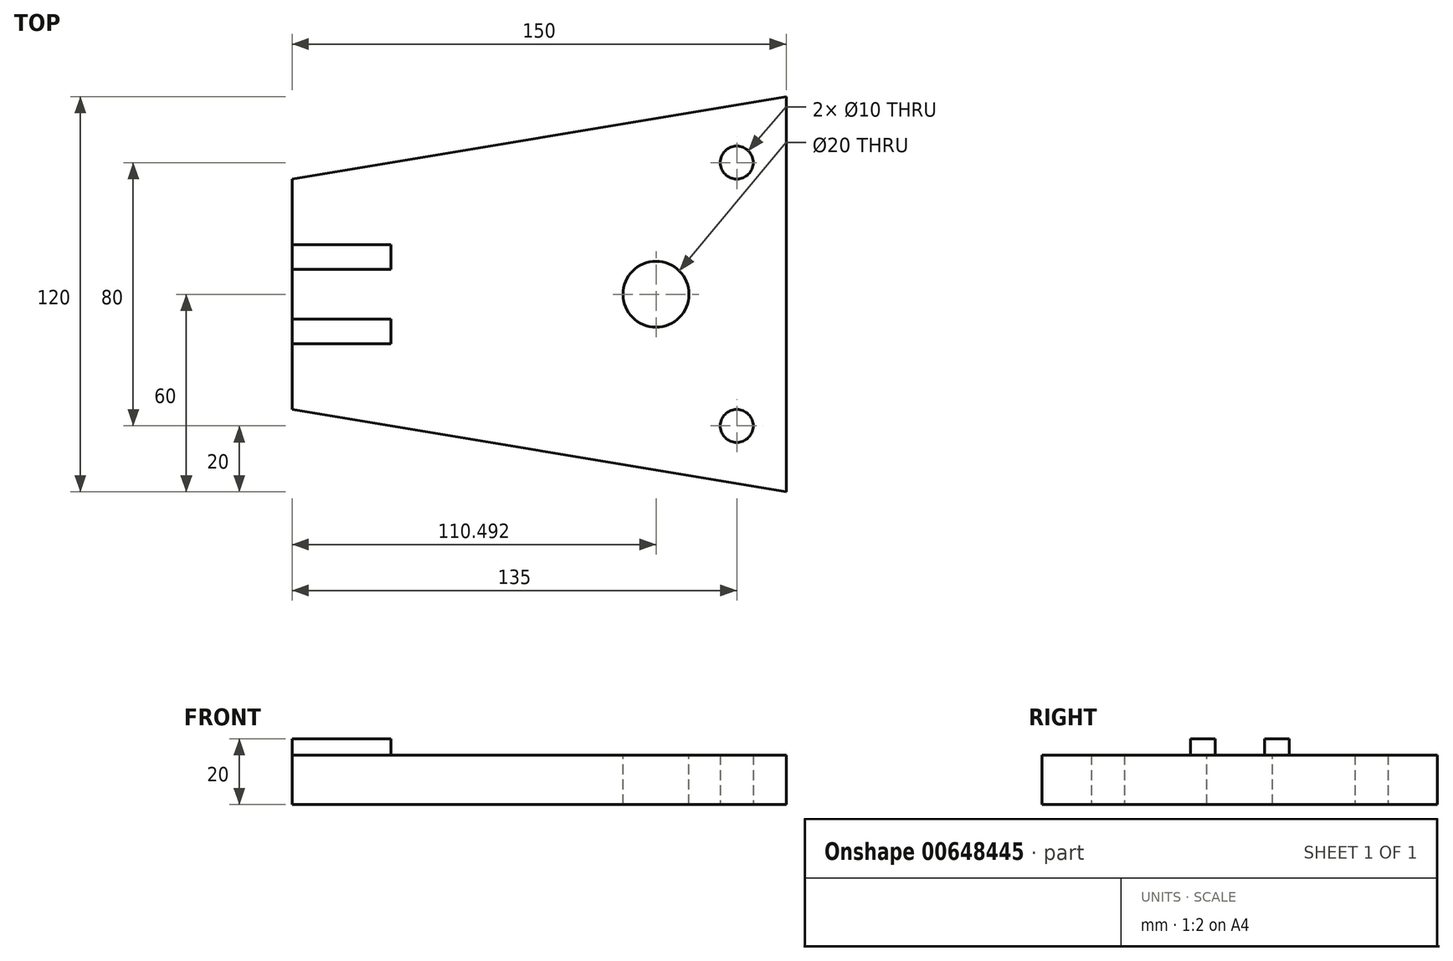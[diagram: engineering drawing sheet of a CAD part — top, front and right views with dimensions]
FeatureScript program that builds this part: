
annotation { "Feature Type Name" : "Feature", "Feature Type Description" : "" }
export const myFeature = defineFeature(function(context is Context, id is Id, definition is map)
    precondition{}
    {
        {
            var Q0;
            Q0=qCreatedBy(makeId("Top.planeOp"),FACE);
            var sketch = newSketch(context, id + "F0", { "sketchPlane" : qUnion([Q0])});
            skLineSegment(sketch, "E0", {"start": v(-135, -35) * mm, "end": v(15, -60) * mm});
            skLineSegment(sketch, "E1", {"start": v(-135, -35) * mm, "end": v(-135, 0) * mm});
            skLineSegment(sketch, "E2", {"start": v(15, -60) * mm, "end": v(15, 0) * mm});
            skCircle(sketch, "E3", {"center": v(0, -40) * mm, "radius": 5 * mm});
            skLineSegment(sketch, "E4.MirrorCS", {"start": v(-135, 35) * mm, "end": v(15, 60) * mm});
            skCircle(sketch, "E5.MirrorC", {"center": v(0, 40) * mm, "radius": 5 * mm});
            skLineSegment(sketch, "E6.MirrorCS", {"start": v(-135, 35) * mm, "end": v(-135, 0) * mm});
            skLineSegment(sketch, "E7.MirrorCS", {"start": v(15, 60) * mm, "end": v(15, 0) * mm});
            skSolve(sketch);
        }
        {
            var Q0;
            Q0=makeQuery(id+"F0.imprint","IMPRINT",FACE,{"disambiguationData":[TD([[makeQuery(id+"F0.imprint","IMPRINT",EDGE,{"derivedFrom":sQuery(id+"F0.wireOp",EDGE,"E0")}),1.0]])]});
            extrude(context, id + "F1", {"entities" : qUnion([Q0]), "depth" : 15 * mm, "offsetDistance" : 25 * mm});
        }
        {
            var Q0;
            Q0=makeQuery(id+"F1.opExtrude","CAP_FACE",FACE,{"disambiguationData":[OSD([sQuery(id+"F0.wireOp",EDGE,"E0"),sQuery(id+"F0.wireOp",EDGE,"E1"),sQuery(id+"F0.wireOp",EDGE,"E2"),sQuery(id+"F0.wireOp",EDGE,"E3"),sQuery(id+"F0.wireOp",EDGE,"E4.MirrorCS"),sQuery(id+"F0.wireOp",EDGE,"E5.MirrorC"),sQuery(id+"F0.wireOp",EDGE,"E6.MirrorCS"),sQuery(id+"F0.wireOp",EDGE,"E7.MirrorCS")])],"isStart":false});
            var sketch = newSketch(context, id + "F2", { "sketchPlane" : qUnion([Q0])});
            skLineSegment(sketch, "E8.bottom", {"start": v(-135, 15) * mm, "end": v(-105, 15) * mm});
            skLineSegment(sketch, "E8.top", {"start": v(-135, -15) * mm, "end": v(-105, -15) * mm});
            skLineSegment(sketch, "E8.left", {"start": v(-135, 15) * mm, "end": v(-135, -15) * mm});
            skLineSegment(sketch, "E8.right", {"start": v(-105, 15) * mm, "end": v(-105, -15) * mm});
            skSolve(sketch);
        }
        {
            var Q0;
            Q0=makeQuery(id+"F2.imprint","IMPRINT",FACE,{"disambiguationData":[TD([[makeQuery(id+"F2.imprint","IMPRINT",EDGE,{"derivedFrom":sQuery(id+"F2.wireOp",EDGE,"E8.bottom")}),-1.0]])]});
            extrude(context, id + "F3", {"entities" : qUnion([Q0]), "operationType" : NewBodyOperationType.ADD, "depth" : 5 * mm, "offsetDistance" : 25 * mm});
        }
        {
            var Q0;
            Q0=makeQuery(id+"F3.opExtrude","CAP_FACE",FACE,{"disambiguationData":[OSD([sQuery(id+"F2.wireOp",EDGE,"E8.bottom"),sQuery(id+"F2.wireOp",EDGE,"E8.top"),sQuery(id+"F2.wireOp",EDGE,"E8.left"),sQuery(id+"F2.wireOp",EDGE,"E8.right")])],"isStart":false});
            var sketch = newSketch(context, id + "F4", { "sketchPlane" : qUnion([Q0])});
            skLineSegment(sketch, "E9.bottom", {"start": v(-135, 7.5) * mm, "end": v(-105, 7.5) * mm});
            skLineSegment(sketch, "E9.top", {"start": v(-135, -7.5) * mm, "end": v(-105, -7.5) * mm});
            skLineSegment(sketch, "E9.left", {"start": v(-135, 7.5) * mm, "end": v(-135, -7.5) * mm});
            skLineSegment(sketch, "E9.right", {"start": v(-105, 7.5) * mm, "end": v(-105, -7.5) * mm});
            skSolve(sketch);
        }
        {
            var Q0;
            Q0 = qSketchRegion(id + "F4", true);
            extrude(context, id + "F5", {"entities" : qUnion([Q0]), "operationType" : NewBodyOperationType.REMOVE, "oppositeDirection" : true, "depth" : 5 * mm, "offsetDistance" : 25 * mm});
        }
        {
            var Q0;
            Q0=makeQuery(id+"F5.boolean.opBoolean","MERGE",FACE,{"derivedFrom":[makeQuery(id+"F1.opExtrude","CAP_FACE",FACE,{"disambiguationData":[OSD([sQuery(id+"F0.wireOp",EDGE,"E0"),sQuery(id+"F0.wireOp",EDGE,"E1"),sQuery(id+"F0.wireOp",EDGE,"E2"),sQuery(id+"F0.wireOp",EDGE,"E3"),sQuery(id+"F0.wireOp",EDGE,"E4.MirrorCS"),sQuery(id+"F0.wireOp",EDGE,"E5.MirrorC"),sQuery(id+"F0.wireOp",EDGE,"E6.MirrorCS"),sQuery(id+"F0.wireOp",EDGE,"E7.MirrorCS")])],"isStart":false}),makeQuery(id+"F5.opExtrude","CAP_FACE",FACE,{"disambiguationData":[OSD([sQuery(id+"F4.wireOp",EDGE,"E9.bottom"),sQuery(id+"F4.wireOp",EDGE,"E9.top"),sQuery(id+"F4.wireOp",EDGE,"E9.left"),sQuery(id+"F4.wireOp",EDGE,"E9.right")])],"isStart":false})]});
            var sketch = newSketch(context, id + "F6", { "sketchPlane" : qUnion([Q0])});
            skCircle(sketch, "E10", {"center": v(-24.5, 0) * mm, "radius": 10 * mm});
            skSolve(sketch);
        }
        {
            var Q0;
            Q0=makeQuery(id+"F6.imprint","IMPRINT",FACE,{"disambiguationData":[TD([[makeQuery(id+"F6.imprint","IMPRINT",EDGE,{"derivedFrom":sQuery(id+"F6.wireOp",EDGE,"E10")}),1.0]])]});
            extrude(context, id + "F7", {"entities" : qUnion([Q0]), "operationType" : NewBodyOperationType.REMOVE, "oppositeDirection" : true, "depth" : 15 * mm, "offsetDistance" : 25 * mm});
        }
    });
